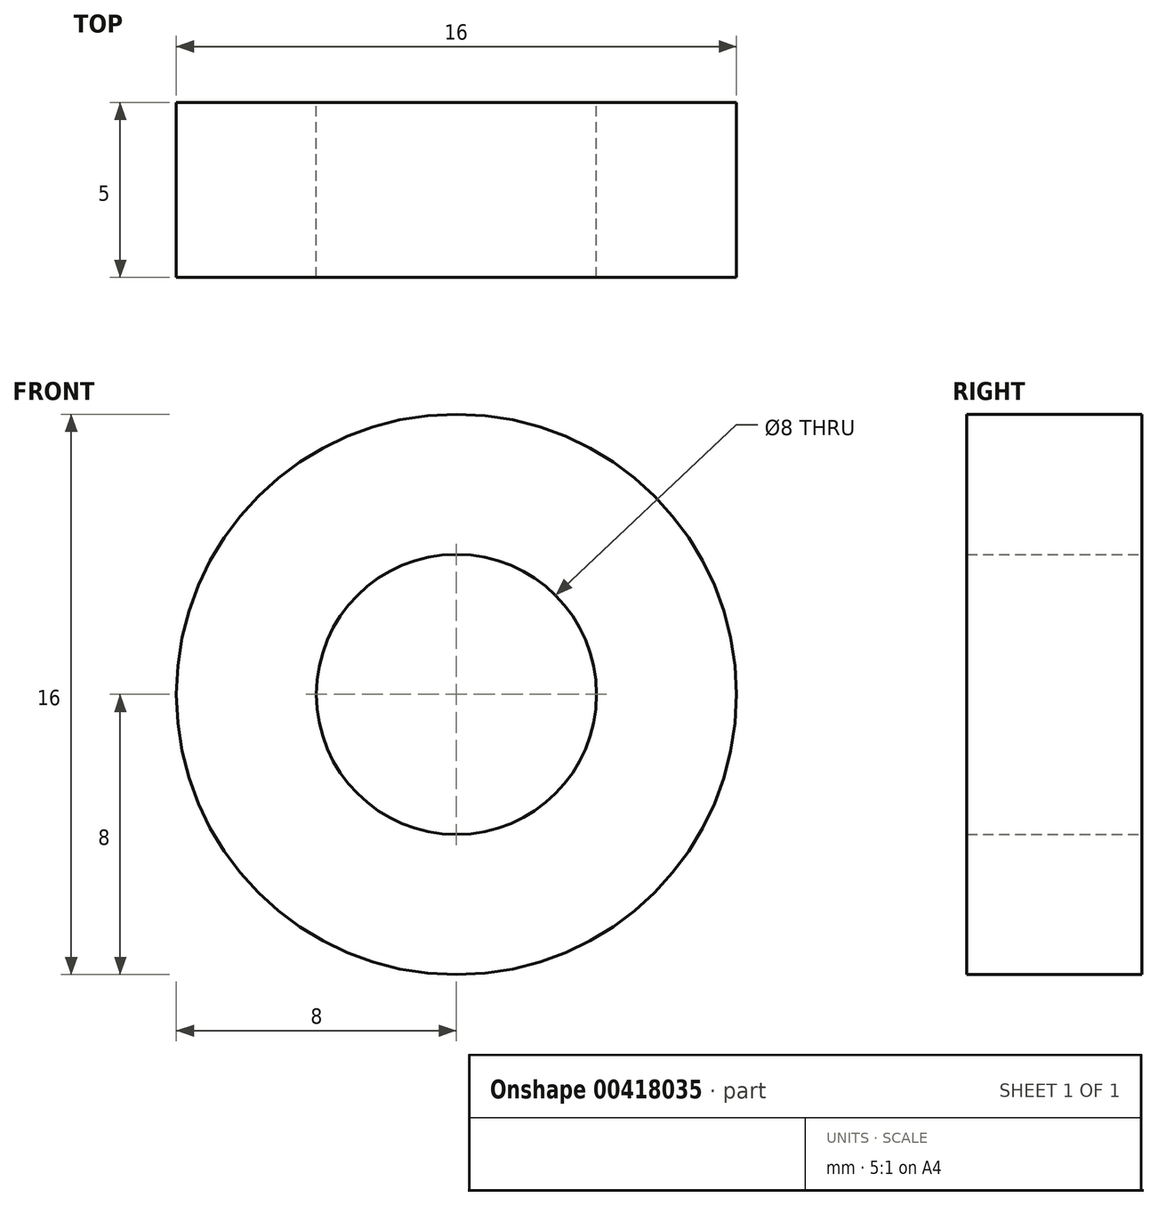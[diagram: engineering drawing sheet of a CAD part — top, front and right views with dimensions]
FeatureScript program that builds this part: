
annotation { "Feature Type Name" : "Feature", "Feature Type Description" : "" }
export const myFeature = defineFeature(function(context is Context, id is Id, definition is map)
    precondition{}
    {
        {
            var Q0;
            Q0=qCreatedBy(makeId("Front.planeOp"),FACE);
            var sketch = newSketch(context, id + "F0", { "sketchPlane" : qUnion([Q0])});
            skCircle(sketch, "E0", {"center": v(0, 0) * mm, "radius": 4 * mm});
            skCircle(sketch, "E1", {"center": v(0, 0) * mm, "radius": 8 * mm});
            skSolve(sketch);
        }
        {
            var Q0;
            Q0=makeQuery(id+"F0.imprint","IMPRINT",FACE,{"disambiguationData":[TD([[makeQuery(id+"F0.imprint","IMPRINT",EDGE,{"derivedFrom":sQuery(id+"F0.wireOp",EDGE,"E0")}),-1.0]])]});
            extrude(context, id + "F1", {"entities" : qUnion([Q0]), "depth" : 5 * mm});
        }
    });
